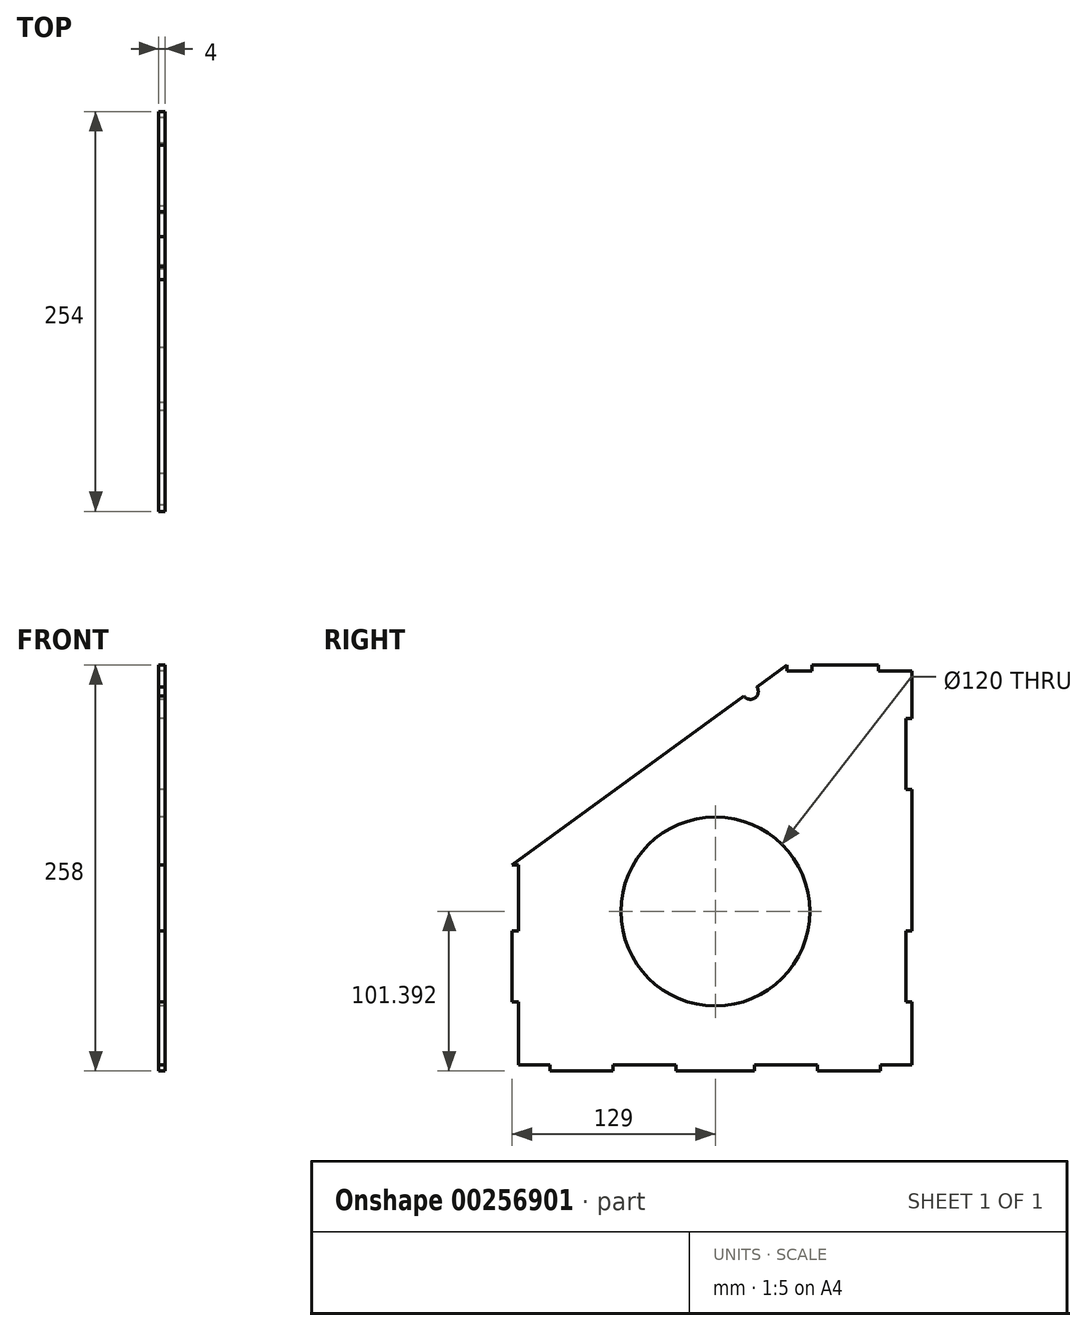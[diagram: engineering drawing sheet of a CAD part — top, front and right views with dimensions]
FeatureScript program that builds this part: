
annotation { "Feature Type Name" : "Feature", "Feature Type Description" : "" }
export const myFeature = defineFeature(function(context is Context, id is Id, definition is map)
    precondition{}
    {
        {
            var Q0;
            Q0=qCreatedBy(makeId("Right.planeOp"),FACE);
            var sketch = newSketch(context, id + "F0", { "sketchPlane" : qUnion([Q0])});
            skLineSegment(sketch, "E0.bottom", {"start": v(0, 0) * mm, "end": v(-20, 0) * mm});
            skLineSegment(sketch, "E0.left", {"start": v(0, 0) * mm, "end": v(0, 40) * mm});
            skLineSegment(sketch, "E1.left", {"start": v(-20, 0) * mm, "end": v(-20, -4) * mm});
            skLineSegment(sketch, "E2.top", {"start": v(-100, -4) * mm, "end": v(-150, -4) * mm});
            skLineSegment(sketch, "E2.left", {"start": v(-100, 0) * mm, "end": v(-100, -4) * mm});
            skLineSegment(sketch, "E2.right", {"start": v(-150, 0) * mm, "end": v(-150, -4) * mm});
            skLineSegment(sketch, "E3.top", {"start": v(-190, -4) * mm, "end": v(-230, -4) * mm});
            skLineSegment(sketch, "E3.left", {"start": v(-190, 0) * mm, "end": v(-190, -4) * mm});
            skLineSegment(sketch, "E3.right", {"start": v(-230, 0) * mm, "end": v(-230, -4) * mm});
            skLineSegment(sketch, "E4", {"start": v(-60, 0) * mm, "end": v(-100, 0) * mm});
            skLineSegment(sketch, "E5", {"start": v(-150, 0) * mm, "end": v(-150, 0) * mm});
            skLineSegment(sketch, "E6", {"start": v(-150, 0) * mm, "end": v(-190, 0) * mm});
            skLineSegment(sketch, "E7", {"start": v(-79.5, 254) * mm, "end": v(-98.67, 240.06) * mm});
            skLineSegment(sketch, "E8", {"start": v(-20, -4) * mm, "end": v(-60, -4) * mm});
            skLineSegment(sketch, "E9", {"start": v(-60, -4) * mm, "end": v(-60, 0) * mm});
            skLineSegment(sketch, "E10", {"start": v(-250, 85) * mm, "end": v(-250, 127.1) * mm});
            skLineSegment(sketch, "E11", {"start": v(-250, 40) * mm, "end": v(-250, 40) * mm});
            skLineSegment(sketch, "E12", {"start": v(0, 40) * mm, "end": v(-4, 40) * mm});
            skLineSegment(sketch, "E13", {"start": v(-4, 40) * mm, "end": v(-4, 85) * mm});
            skLineSegment(sketch, "E14", {"start": v(-4, 85) * mm, "end": v(0, 85) * mm});
            skLineSegment(sketch, "E15", {"start": v(0, 220) * mm, "end": v(-4, 220) * mm});
            skLineSegment(sketch, "E16", {"start": v(-4, 220) * mm, "end": v(-4, 175) * mm});
            skLineSegment(sketch, "E17", {"start": v(-4, 175) * mm, "end": v(0, 175) * mm});
            skLineSegment(sketch, "E18", {"start": v(0, 220) * mm, "end": v(0, 250) * mm});
            skLineSegment(sketch, "E19", {"start": v(0, 85) * mm, "end": v(0, 175) * mm});
            skLineSegment(sketch, "E20", {"start": v(-230, 0) * mm, "end": v(-250, 0) * mm});
            skLineSegment(sketch, "E21", {"start": v(-250, 40) * mm, "end": v(-250, 0) * mm});
            skLineSegment(sketch, "E22", {"start": v(0, 250) * mm, "end": v(-21.25, 250) * mm});
            skLineSegment(sketch, "E23", {"start": v(-63.75, 250) * mm, "end": v(-79.5, 250) * mm});
            skLineSegment(sketch, "E24", {"start": v(-21.25, 250) * mm, "end": v(-21.25, 254) * mm});
            skLineSegment(sketch, "E25", {"start": v(-21.25, 254) * mm, "end": v(-63.75, 254) * mm});
            skPoint(sketch, "E25.endSnap0", {"position": v(-63.75, 250) * mm});
            skLineSegment(sketch, "E26", {"start": v(-63.75, 254) * mm, "end": v(-63.75, 250) * mm});
            skLineSegment(sketch, "E27", {"start": v(-79.5, 254) * mm, "end": v(-79.5, 250) * mm});
            skLineSegment(sketch, "E28", {"start": v(-250, 85) * mm, "end": v(-254, 85) * mm});
            skLineSegment(sketch, "E29", {"start": v(-254, 85) * mm, "end": v(-254, 40) * mm});
            skLineSegment(sketch, "E30", {"start": v(-254, 40) * mm, "end": v(-250, 40) * mm});
            skLineSegment(sketch, "E31", {"start": v(-254, 127.1) * mm, "end": v(-250, 127.1) * mm});
            skArc(sketch, "E32", {"start": v(-106.76, 234.17) * mm, "mid": v(-99.78, 233.07) * mm, "end": v(-98.67, 240.06) * mm});
            skLineSegment(sketch, "E33.trimOffspring", {"start": v(-106.76, 234.17) * mm, "end": v(-254, 127.1) * mm});
            skSolve(sketch);
        }
        {
            var Q0;
            Q0=makeQuery(id+"F0.imprint","IMPRINT",FACE,{"disambiguationData":[TD([[makeQuery(id+"F0.imprint","IMPRINT",EDGE,{"derivedFrom":sQuery(id+"F0.wireOp",EDGE,"E0.bottom")}),-1.0]])]});
            extrude(context, id + "F1", {"entities" : qUnion([Q0]), "depth" : 4 * mm});
        }
        {
            var Q0;
            Q0=makeQuery(id+"F1.opExtrude","CAP_FACE",FACE,{"disambiguationData":[OSD([sQuery(id+"F0.wireOp",EDGE,"E0.bottom"),sQuery(id+"F0.wireOp",EDGE,"E0.left"),sQuery(id+"F0.wireOp",EDGE,"E1.left"),sQuery(id+"F0.wireOp",EDGE,"E2.top"),sQuery(id+"F0.wireOp",EDGE,"E2.left"),sQuery(id+"F0.wireOp",EDGE,"E2.right"),sQuery(id+"F0.wireOp",EDGE,"E3.top"),sQuery(id+"F0.wireOp",EDGE,"E3.left"),sQuery(id+"F0.wireOp",EDGE,"E3.right"),sQuery(id+"F0.wireOp",EDGE,"E4"),sQuery(id+"F0.wireOp",EDGE,"E6"),sQuery(id+"F0.wireOp",EDGE,"E7"),sQuery(id+"F0.wireOp",EDGE,"Ny4hH3fG-H4GL-R5oq-Go1v-iJF5zvyQumog"),sQuery(id+"F0.wireOp",EDGE,"mf5psRB7-I0Cn-EgLD-jKxY-mCNBJTjqWHxF"),sQuery(id+"F0.wireOp",EDGE,"bNbiPylh-YCr3-da4V-WFlo-lDtDUwVRmCHg"),sQuery(id+"F0.wireOp",EDGE,"E8"),sQuery(id+"F0.wireOp",EDGE,"E9"),sQuery(id+"F0.wireOp",EDGE,"E10"),sQuery(id+"F0.wireOp",EDGE,"E12"),sQuery(id+"F0.wireOp",EDGE,"E13"),sQuery(id+"F0.wireOp",EDGE,"E14"),sQuery(id+"F0.wireOp",EDGE,"E15"),sQuery(id+"F0.wireOp",EDGE,"E16"),sQuery(id+"F0.wireOp",EDGE,"E17"),sQuery(id+"F0.wireOp",EDGE,"E18"),sQuery(id+"F0.wireOp",EDGE,"E19"),sQuery(id+"F0.wireOp",EDGE,"E20"),sQuery(id+"F0.wireOp",EDGE,"E21"),sQuery(id+"F0.wireOp",EDGE,"E22"),sQuery(id+"F0.wireOp",EDGE,"vhuMehFY-gTZD-huO7-waoA-9P1PBl7xOcwt")])],"isStart":true});
            var sketch = newSketch(context, id + "F2", { "sketchPlane" : qUnion([Q0])});
            skCircle(sketch, "E34", {"center": v(125, 97.4) * mm, "radius": 60 * mm});
            skPoint(sketch, "E34.centerSnap0", {"position": v(125, -4) * mm});
            skSolve(sketch);
        }
        {
            var Q0;
            Q0 = qSketchRegion(id + "F2", true);
            extrude(context, id + "F3", {"entities" : qUnion([Q0]), "operationType" : NewBodyOperationType.REMOVE, "oppositeDirection" : true, "depth" : 25 * mm});
        }
    });
